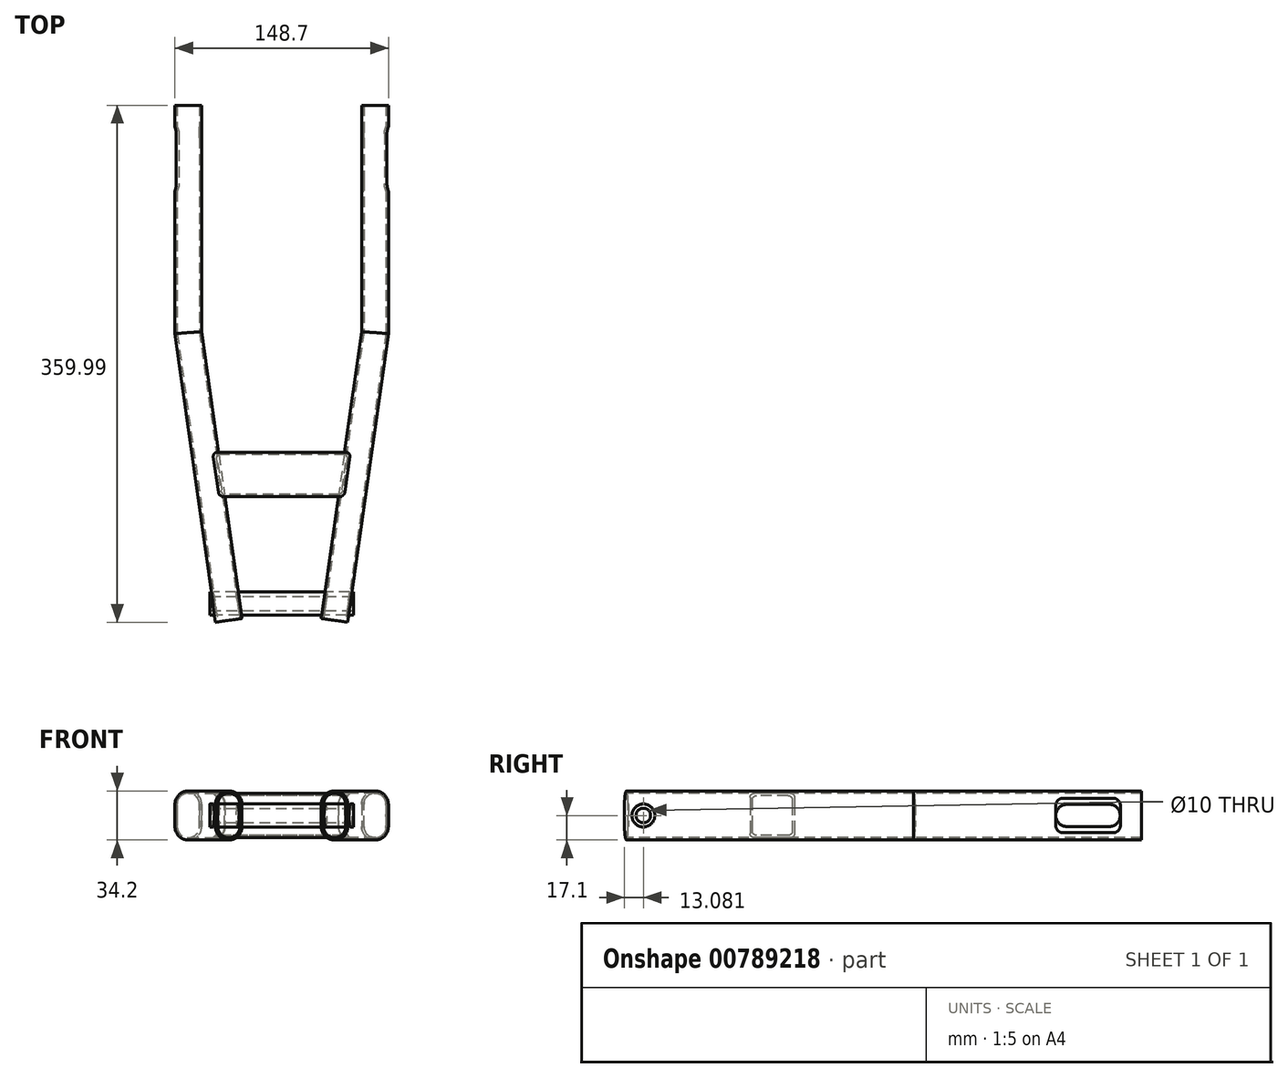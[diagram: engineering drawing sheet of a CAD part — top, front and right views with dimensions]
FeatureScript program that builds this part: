
annotation { "Feature Type Name" : "Feature", "Feature Type Description" : "" }
export const myFeature = defineFeature(function(context is Context, id is Id, definition is map)
    precondition{}
    {
        {
            var Q0;
            Q0=qCreatedBy(makeId("Front.planeOp"),FACE);
            var sketch = newSketch(context, id + "F0", { "sketchPlane" : qUnion([Q0])});
            skLineSegment(sketch, "E0.left", {"start": v(-57.25, -7.75) * mm, "end": v(-57.25, 7.75) * mm});
            skLineSegment(sketch, "E0.right", {"start": v(-72.75, -7.75) * mm, "end": v(-72.75, 7.75) * mm});
            skPoint(sketch, "E0.middle", {"position": v(-65, 0) * mm});
            skArc(sketch, "E1", {"start": v(-57.25, 7.75) * mm, "mid": v(-65, 15.5) * mm, "end": v(-72.75, 7.75) * mm});
            skArc(sketch, "E2", {"start": v(-72.75, -7.75) * mm, "mid": v(-65, -15.5) * mm, "end": v(-57.25, -7.75) * mm});
            skLineSegment(sketch, "E3", {"start": v(-55.65, 7.75) * mm, "end": v(-55.65, -7.75) * mm});
            skLineSegment(sketch, "E4", {"start": v(-74.35, 7.75) * mm, "end": v(-74.35, -7.75) * mm});
            skArc(sketch, "E5", {"start": v(-55.65, 7.75) * mm, "mid": v(-65, 17.1) * mm, "end": v(-74.35, 7.75) * mm});
            skArc(sketch, "E6", {"start": v(-74.35, -7.75) * mm, "mid": v(-65, -17.1) * mm, "end": v(-55.65, -7.75) * mm});
            skSolve(sketch);
        }
        {
            var Q0;
            Q0=qCreatedBy(makeId("Top.planeOp"),FACE);
            var sketch = newSketch(context, id + "F1", { "sketchPlane" : qUnion([Q0])});
            skLineSegment(sketch, "E7", {"start": v(-65, 0) * mm, "end": v(-65, -158.3) * mm});
            skLineSegment(sketch, "E8", {"start": v(-65, -158.3) * mm, "end": v(-36.84, -358.7) * mm});
            skSolve(sketch);
        }
        {
            var Q0;
            Q0 = qSketchRegion(id + "F0", true);
            var Q1;
            Q1=sQuery(id+"F1.wireOp",EDGE,"E7");
            var Q2;
            Q2=sQuery(id+"F1.wireOp",EDGE,"E8");
            sweep(context, id + "F2", {"profiles" : qUnion([Q0]), "path" : qUnion([Q1, Q2])});
        }
        {
            var Q0;
            Q0=makeQuery(id+"F2.opSweep","SWEPT_BODY",BODY,{"disambiguationData":[OSD([sQuery(id+"F0.wireOp",EDGE,"E0.left"),sQuery(id+"F0.wireOp",EDGE,"E0.right"),sQuery(id+"F0.wireOp",EDGE,"E1"),sQuery(id+"F0.wireOp",EDGE,"E2"),sQuery(id+"F0.wireOp",EDGE,"E3"),sQuery(id+"F0.wireOp",EDGE,"E4"),sQuery(id+"F0.wireOp",EDGE,"E5"),sQuery(id+"F0.wireOp",EDGE,"E6"),sQuery(id+"F1.wireOp",EDGE,"E8")])]});
            var Q1;
            Q1=qCreatedBy(makeId("Right.planeOp"),FACE);
            mirror(context, id + "F3", {"operationType" : NewBodyOperationType.ADD, "entities" : qUnion([Q0]), "mirrorPlane" : qUnion([Q1])});
        }
        {
            var Q0;
            Q0=qCreatedBy(makeId("Right.planeOp"),FACE);
            var sketch = newSketch(context, id + "F4", { "sketchPlane" : qUnion([Q0])});
            skCircle(sketch, "E9", {"center": v(-346.9, 0) * mm, "radius": 8 * mm});
            skSolve(sketch);
        }
        {
            var Q0;
            Q0 = qSketchRegion(id + "F4", true);
            extrude(context, id + "F5", {"entities" : qUnion([Q0]), "operationType" : NewBodyOperationType.ADD, "endBound" : BoundingType.SYMMETRIC, "depth" : 100 * mm, "offsetDistance" : 25 * mm});
        }
        {
            var Q0;
            Q0=makeQuery(id+"F5.opExtrude","CAP_FACE",FACE,{"disambiguationData":[OSD([sQuery(id+"F4.wireOp",EDGE,"E9")])],"isStart":false});
            var sketch = newSketch(context, id + "F6", { "sketchPlane" : qUnion([Q0])});
            skCircle(sketch, "E10", {"center": v(-346.9, 0) * mm, "radius": 5 * mm});
            skSolve(sketch);
        }
        {
            var Q0;
            Q0 = qSketchRegion(id + "F6", true);
            extrude(context, id + "F7", {"entities" : qUnion([Q0]), "operationType" : NewBodyOperationType.REMOVE, "oppositeDirection" : true, "depth" : 110 * mm, "offsetDistance" : 25 * mm});
        }
        {
            var Q0;
            Q0=qCreatedBy(makeId("Right.planeOp"),FACE);
            var sketch = newSketch(context, id + "F8", { "sketchPlane" : qUnion([Q0])});
            skLineSegment(sketch, "E11.bottom", {"start": v(-244.58, -15.5) * mm, "end": v(-269.58, -15.5) * mm});
            skLineSegment(sketch, "E11.top", {"start": v(-244.58, 15.5) * mm, "end": v(-269.58, 15.5) * mm});
            skLineSegment(sketch, "E11.left", {"start": v(-241.58, -12.5) * mm, "end": v(-241.58, 12.5) * mm});
            skLineSegment(sketch, "E11.right", {"start": v(-272.58, -12.5) * mm, "end": v(-272.58, 12.5) * mm});
            skPoint(sketch, "E11.middle", {"position": v(-257.08, 0) * mm});
            skLineSegment(sketch, "E12", {"start": v(-267.98, -13.9) * mm, "end": v(-246.18, -13.9) * mm});
            skLineSegment(sketch, "E13", {"start": v(-243.18, -10.9) * mm, "end": v(-243.18, 10.9) * mm});
            skLineSegment(sketch, "E14", {"start": v(-246.18, 13.9) * mm, "end": v(-267.98, 13.9) * mm});
            skPoint(sketch, "E15.start.orphan", {"position": v(-270.98, 8.3) * mm});
            skLineSegment(sketch, "E16", {"start": v(-270.98, 10.9) * mm, "end": v(-270.98, -10.9) * mm});
            skPoint(sketch, "E17.visualSharp", {"position": v(-241.58, 15.5) * mm});
            skArc(sketch, "E17.filletArc", {"start": v(-241.58, 12.5) * mm, "mid": v(-242.46, 14.62) * mm, "end": v(-244.58, 15.5) * mm});
            skPoint(sketch, "E18.visualSharp", {"position": v(-241.58, -15.5) * mm});
            skArc(sketch, "E18.filletArc", {"start": v(-244.58, -15.5) * mm, "mid": v(-242.46, -14.62) * mm, "end": v(-241.58, -12.5) * mm});
            skPoint(sketch, "E19.visualSharp", {"position": v(-272.58, -15.5) * mm});
            skArc(sketch, "E19.filletArc", {"start": v(-272.58, -12.5) * mm, "mid": v(-271.7, -14.62) * mm, "end": v(-269.58, -15.5) * mm});
            skPoint(sketch, "E20.visualSharp", {"position": v(-272.58, 15.5) * mm});
            skArc(sketch, "E20.filletArc", {"start": v(-269.58, 15.5) * mm, "mid": v(-271.7, 14.62) * mm, "end": v(-272.58, 12.5) * mm});
            skPoint(sketch, "E21.visualSharp", {"position": v(-270.98, 13.9) * mm});
            skArc(sketch, "E21.filletArc", {"start": v(-267.98, 13.9) * mm, "mid": v(-270.1, 13.02) * mm, "end": v(-270.98, 10.9) * mm});
            skPoint(sketch, "E22.visualSharp", {"position": v(-243.18, 13.9) * mm});
            skArc(sketch, "E22.filletArc", {"start": v(-243.18, 10.9) * mm, "mid": v(-244.06, 13.02) * mm, "end": v(-246.18, 13.9) * mm});
            skPoint(sketch, "E23.visualSharp", {"position": v(-270.98, -13.9) * mm});
            skArc(sketch, "E23.filletArc", {"start": v(-270.98, -10.9) * mm, "mid": v(-270.1, -13.02) * mm, "end": v(-267.98, -13.9) * mm});
            skPoint(sketch, "E24.visualSharp", {"position": v(-243.18, -13.9) * mm});
            skArc(sketch, "E24.filletArc", {"start": v(-246.18, -13.9) * mm, "mid": v(-244.06, -13.02) * mm, "end": v(-243.18, -10.9) * mm});
            skSolve(sketch);
        }
        {
            var Q0;
            {var subQ0=sQuery(id+"F1.wireOp",EDGE,"E7");var subQ4=sQuery(id+"F0.wireOp",EDGE,"E4");Q0=makeQuery(id+"F5Wy97pS9RI03tn_1.boolean.opBoolean","SPLIT",FACE,{"disambiguationData":[TD([makeQuery(id+"F5Wy97pS9RI03tn_1.opExtrude","SWEPT_FACE",FACE,{"disambiguationData":[OSD([sQuery(id+"FOhX2ZVzm9cz6Cf_1.wireOp",EDGE,"FVpH9jkE-RjFi-ig4O-xtVg-mI0b15cMh8i4")])]})])],"derivedFrom":makeQuery(id+"F3.opPattern","COPY",FACE,{"derivedFrom":makeQuery(id+"F2.opSweep","SWEPT_FACE",FACE,{"disambiguationData":[OSD([subQ4,subQ0])]}),"instanceName":"1"})});}
            cPlane(context, id + "F9", {"entities" : qUnion([Q0]), "cplaneType" : CPlaneType.OFFSET, "offset" : 25 * mm, "width" : 150 * mm, "height" : 150 * mm});
        }
        {
            var Q0;
            Q0 = qSketchRegion(id + "F8", true);
            var Q1;
            Q1=makeQuery(id+"F2.opSweep","SWEPT_BODY",BODY,{"disambiguationData":[OSD([sQuery(id+"F0.wireOp",EDGE,"E0.left"),sQuery(id+"F0.wireOp",EDGE,"E0.right"),sQuery(id+"F0.wireOp",EDGE,"E1"),sQuery(id+"F0.wireOp",EDGE,"E2"),sQuery(id+"F0.wireOp",EDGE,"E3"),sQuery(id+"F0.wireOp",EDGE,"E4"),sQuery(id+"F0.wireOp",EDGE,"E5"),sQuery(id+"F0.wireOp",EDGE,"E6"),sQuery(id+"F1.wireOp",EDGE,"E8")])]});
            extrude(context, id + "F10", {"entities" : qUnion([Q0]), "operationType" : NewBodyOperationType.ADD, "endBound" : BoundingType.UP_TO_BODY, "depth" : 25 * mm, "endBoundEntityBody" : qUnion([Q1]), "offsetDistance" : 25 * mm});
        }
        {
            var Q0;
            Q0 = qSketchRegion(id + "F8", true);
            var Q1;
            Q1=makeQuery(id+"F2.opSweep","SWEPT_BODY",BODY,{"disambiguationData":[OSD([sQuery(id+"F0.wireOp",EDGE,"E0.left"),sQuery(id+"F0.wireOp",EDGE,"E0.right"),sQuery(id+"F0.wireOp",EDGE,"E1"),sQuery(id+"F0.wireOp",EDGE,"E2"),sQuery(id+"F0.wireOp",EDGE,"E3"),sQuery(id+"F0.wireOp",EDGE,"E4"),sQuery(id+"F0.wireOp",EDGE,"E5"),sQuery(id+"F0.wireOp",EDGE,"E6"),sQuery(id+"F1.wireOp",EDGE,"E8")])]});
            extrude(context, id + "F11", {"entities" : qUnion([Q0]), "operationType" : NewBodyOperationType.ADD, "endBound" : BoundingType.UP_TO_BODY, "oppositeDirection" : true, "depth" : 25 * mm, "endBoundEntityBody" : qUnion([Q1]), "offsetDistance" : 25 * mm});
        }
        {
            var Q0;
            Q0=makeQuery(id+"F3.opPattern","COPY",FACE,{"derivedFrom":makeQuery(id+"F2.opSweep","SWEPT_FACE",FACE,{"disambiguationData":[OSD([sQuery(id+"F0.wireOp",EDGE,"E4"),sQuery(id+"F1.wireOp",EDGE,"E7")])]}),"instanceName":"1"});
            var sketch = newSketch(context, id + "F12", { "sketchPlane" : qUnion([Q0])});
            skLineSegment(sketch, "E25.bottom", {"start": v(-22.54, -7.75) * mm, "end": v(-52.04, -7.75) * mm});
            skLineSegment(sketch, "E25.top", {"start": v(-22.54, 7.75) * mm, "end": v(-52.04, 7.75) * mm});
            skPoint(sketch, "E25.middle", {"position": v(-37.29, 0) * mm});
            skArc(sketch, "E26", {"start": v(-22.54, -7.75) * mm, "mid": v(-14.79, 0) * mm, "end": v(-22.54, 7.75) * mm});
            skArc(sketch, "E27", {"start": v(-52.04, 7.75) * mm, "mid": v(-59.79, 0) * mm, "end": v(-52.04, -7.75) * mm});
            skSolve(sketch);
        }
        {
            var Q0;
            Q0 = qSketchRegion(id + "F12", true);
            extrude(context, id + "F13", {"entities" : qUnion([Q0]), "operationType" : NewBodyOperationType.REMOVE, "oppositeDirection" : true, "depth" : 25 * mm, "offsetDistance" : 25 * mm});
        }
        {
            var Q0;
            Q0=makeQuery(id+"F2.opSweep","SWEPT_FACE",FACE,{"disambiguationData":[OSD([sQuery(id+"F0.wireOp",EDGE,"E4"),sQuery(id+"F1.wireOp",EDGE,"E7")])]});
            var sketch = newSketch(context, id + "F14", { "sketchPlane" : qUnion([Q0])});
            skLineSegment(sketch, "E28.bottom", {"start": v(52.04, -7.75) * mm, "end": v(22.54, -7.75) * mm});
            skLineSegment(sketch, "E28.top", {"start": v(52.04, 7.75) * mm, "end": v(22.54, 7.75) * mm});
            skPoint(sketch, "E28.middle", {"position": v(37.3, 0) * mm});
            skArc(sketch, "E29", {"start": v(22.54, 7.75) * mm, "mid": v(14.79, 0) * mm, "end": v(22.54, -7.75) * mm});
            skArc(sketch, "E30", {"start": v(52.04, -7.75) * mm, "mid": v(59.8, 0) * mm, "end": v(52.04, 7.75) * mm});
            skSolve(sketch);
        }
        {
            var Q0;
            Q0 = qSketchRegion(id + "F14", true);
            extrude(context, id + "F15", {"entities" : qUnion([Q0]), "operationType" : NewBodyOperationType.REMOVE, "oppositeDirection" : true, "depth" : 25 * mm, "offsetDistance" : 25 * mm});
        }
        {
            var Q0;
            Q0=qCreatedBy(id+"F9.planeOp",FACE);
            var sketch = newSketch(context, id + "F16", { "sketchPlane" : qUnion([Q0])});
            skLineSegment(sketch, "E31.bottom", {"start": v(-19.76, -12) * mm, "end": v(-54.76, -12) * mm});
            skLineSegment(sketch, "E31.top", {"start": v(-19.76, 12) * mm, "end": v(-54.76, 12) * mm});
            skLineSegment(sketch, "E31.left", {"start": v(-14.76, -7) * mm, "end": v(-14.76, 7) * mm});
            skLineSegment(sketch, "E31.right", {"start": v(-59.76, -7) * mm, "end": v(-59.76, 7) * mm});
            skPoint(sketch, "E31.middle", {"position": v(-37.26, 0) * mm});
            skPoint(sketch, "E32.visualSharp", {"position": v(-59.76, 12) * mm});
            skArc(sketch, "E32.filletArc", {"start": v(-54.76, 12) * mm, "mid": v(-58.3, 10.54) * mm, "end": v(-59.76, 7) * mm});
            skPoint(sketch, "E33.visualSharp", {"position": v(-14.76, 12) * mm});
            skArc(sketch, "E33.filletArc", {"start": v(-14.76, 7) * mm, "mid": v(-16.22, 10.54) * mm, "end": v(-19.76, 12) * mm});
            skPoint(sketch, "E34.visualSharp", {"position": v(-14.76, -12) * mm});
            skArc(sketch, "E34.filletArc", {"start": v(-19.76, -12) * mm, "mid": v(-16.22, -10.54) * mm, "end": v(-14.76, -7) * mm});
            skPoint(sketch, "E35.visualSharp", {"position": v(-59.76, -12) * mm});
            skArc(sketch, "E35.filletArc", {"start": v(-59.76, -7) * mm, "mid": v(-58.3, -10.54) * mm, "end": v(-54.76, -12) * mm});
            skSolve(sketch);
        }
        {
            var Q0;
            Q0 = qSketchRegion(id + "F16", true);
            extrude(context, id + "F17", {"entities" : qUnion([Q0]), "operationType" : NewBodyOperationType.REMOVE, "oppositeDirection" : true, "depth" : 35 * mm, "offsetDistance" : 25 * mm});
        }
        {
            var Q0;
            {var subQ0=sQuery(id+"F1.wireOp",EDGE,"E7");var subQ4=sQuery(id+"F0.wireOp",EDGE,"E4");Q0=makeQuery(id+"F15.boolean.opBoolean","SPLIT",FACE,{"disambiguationData":[TD([makeQuery(id+"F15.opExtrude","SWEPT_FACE",FACE,{"disambiguationData":[OSD([sQuery(id+"F14.wireOp",EDGE,"E30")])]})])],"derivedFrom":makeQuery(id+"F2.opSweep","SWEPT_FACE",FACE,{"disambiguationData":[OSD([subQ4,subQ0])]})});}
            cPlane(context, id + "F18", {"entities" : qUnion([Q0]), "cplaneType" : CPlaneType.OFFSET, "offset" : 25 * mm, "width" : 150 * mm, "height" : 150 * mm});
        }
        {
            var Q0;
            Q0=qCreatedBy(id+"F18.planeOp",FACE);
            var sketch = newSketch(context, id + "F19", { "sketchPlane" : qUnion([Q0])});
            skLineSegment(sketch, "E36.bottom", {"start": v(54.76, -12) * mm, "end": v(19.76, -12) * mm});
            skLineSegment(sketch, "E36.top", {"start": v(54.76, 12) * mm, "end": v(19.76, 12) * mm});
            skLineSegment(sketch, "E36.left", {"start": v(59.76, -7) * mm, "end": v(59.76, 7) * mm});
            skLineSegment(sketch, "E36.right", {"start": v(14.76, -7) * mm, "end": v(14.76, 7) * mm});
            skPoint(sketch, "E36.middle", {"position": v(37.26, 0) * mm});
            skPoint(sketch, "E37.visualSharp", {"position": v(14.76, 12) * mm});
            skArc(sketch, "E37.filletArc", {"start": v(19.76, 12) * mm, "mid": v(16.22, 10.54) * mm, "end": v(14.76, 7) * mm});
            skPoint(sketch, "E38.visualSharp", {"position": v(59.76, 12) * mm});
            skArc(sketch, "E38.filletArc", {"start": v(59.76, 7) * mm, "mid": v(58.3, 10.54) * mm, "end": v(54.76, 12) * mm});
            skPoint(sketch, "E39.visualSharp", {"position": v(59.76, -12) * mm});
            skArc(sketch, "E39.filletArc", {"start": v(54.76, -12) * mm, "mid": v(58.3, -10.54) * mm, "end": v(59.76, -7) * mm});
            skPoint(sketch, "E40.visualSharp", {"position": v(14.76, -12) * mm});
            skArc(sketch, "E40.filletArc", {"start": v(14.76, -7) * mm, "mid": v(16.22, -10.54) * mm, "end": v(19.76, -12) * mm});
            skSolve(sketch);
        }
        {
            var Q0;
            Q0 = qSketchRegion(id + "F19", true);
            extrude(context, id + "F20", {"entities" : qUnion([Q0]), "operationType" : NewBodyOperationType.REMOVE, "oppositeDirection" : true, "depth" : 35 * mm, "offsetDistance" : 25 * mm});
        }
    });
